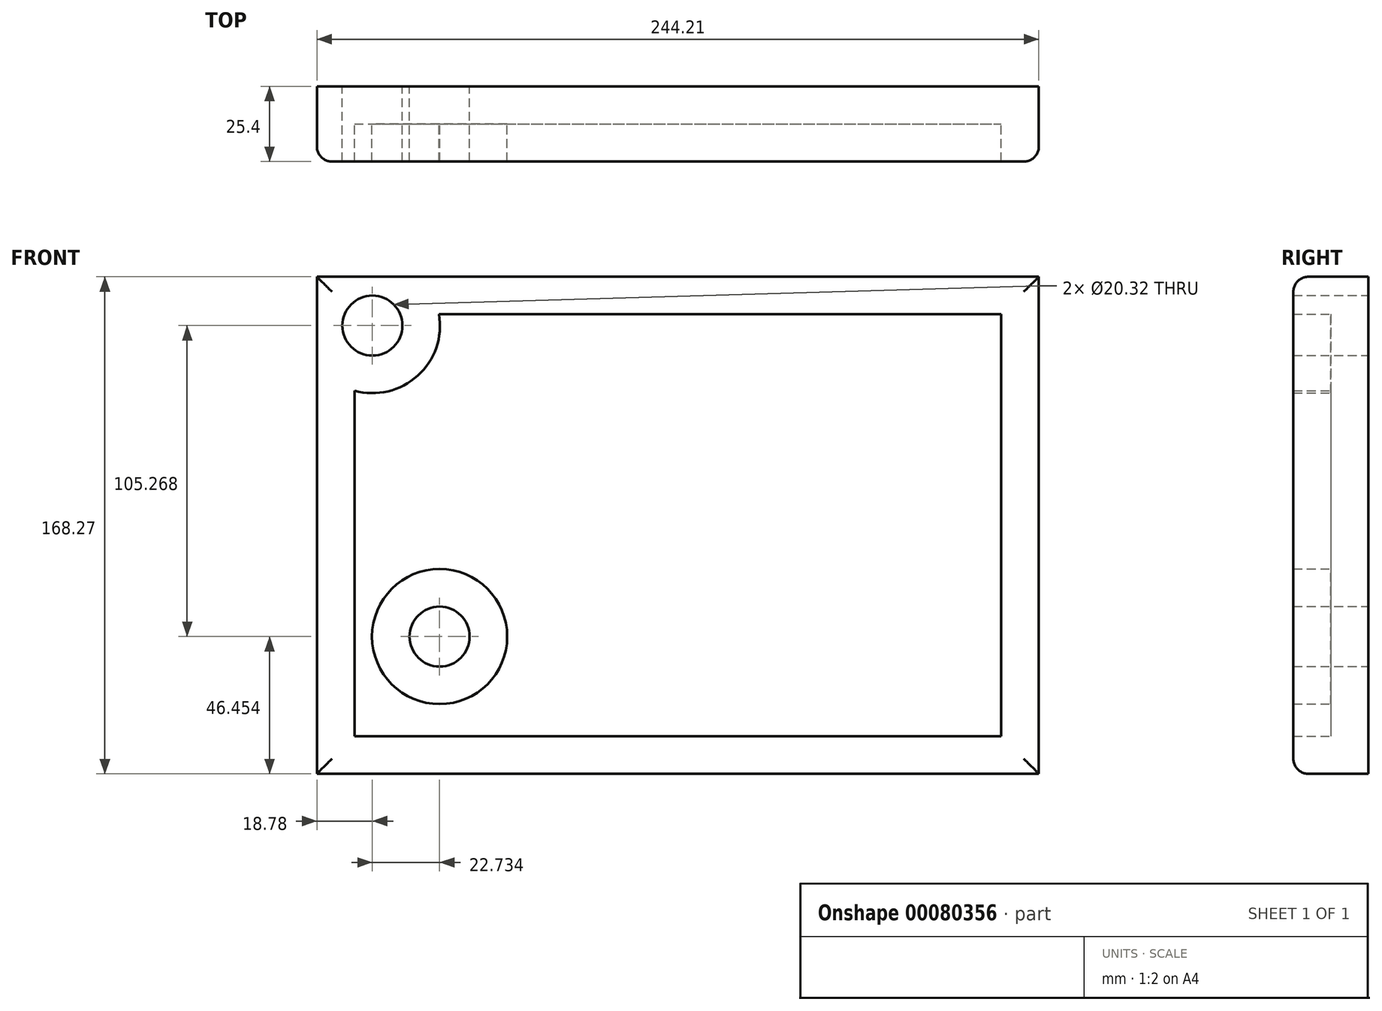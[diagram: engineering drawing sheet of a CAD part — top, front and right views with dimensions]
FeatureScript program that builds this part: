
annotation { "Feature Type Name" : "Feature", "Feature Type Description" : "" }
export const myFeature = defineFeature(function(context is Context, id is Id, definition is map)
    precondition{}
    {
        {
            var Q0;
            Q0=qCreatedBy(makeId("Front.planeOp"),FACE);
            var sketch = newSketch(context, id + "F0", { "sketchPlane" : qUnion([Q0])});
            skLineSegment(sketch, "E0.bottom", {"start": v(-105.93, 86.8) * mm, "end": v(138.28, 86.8) * mm});
            skLineSegment(sketch, "E0.top", {"start": v(-105.93, -81.47) * mm, "end": v(138.28, -81.47) * mm});
            skLineSegment(sketch, "E0.left", {"start": v(-105.93, 86.8) * mm, "end": v(-105.93, -81.47) * mm});
            skLineSegment(sketch, "E0.right", {"start": v(138.28, 86.8) * mm, "end": v(138.28, -81.47) * mm});
            skCircle(sketch, "E1", {"center": v(-87.15, 70.25) * mm, "radius": 10.16 * mm});
            skCircle(sketch, "E2", {"center": v(-64.42, -35.02) * mm, "radius": 10.16 * mm});
            skSolve(sketch);
        }
        {
            var Q0;
            Q0=makeQuery(id+"F0.imprint","IMPRINT",FACE,{"disambiguationData":[TD([[makeQuery(id+"F0.imprint","IMPRINT",EDGE,{"derivedFrom":sQuery(id+"F0.wireOp",EDGE,"E0.bottom")}),-1.0]])]});
            extrude(context, id + "F1", {"entities" : qUnion([Q0]), "depth" : 25.4 * mm});
        }
        {
            var Q0;
            Q0=makeQuery(id+"F1.opExtrude","CAP_EDGE",EDGE,{"disambiguationData":[OSD([sQuery(id+"F0.wireOp",EDGE,"E0.bottom")])],"isStart":false});
            var Q1;
            Q1=makeQuery(id+"F1.opExtrude","CAP_EDGE",EDGE,{"disambiguationData":[OSD([sQuery(id+"F0.wireOp",EDGE,"E0.left")])],"isStart":false});
            var Q2;
            Q2=makeQuery(id+"F1.opExtrude","CAP_EDGE",EDGE,{"disambiguationData":[OSD([sQuery(id+"F0.wireOp",EDGE,"E0.top")])],"isStart":false});
            var Q3;
            Q3=makeQuery(id+"F1.opExtrude","CAP_EDGE",EDGE,{"disambiguationData":[OSD([sQuery(id+"F0.wireOp",EDGE,"E0.right")])],"isStart":false});
            fillet(context, id + "F2", {"entities" : qUnion([Q0, Q1, Q2, Q3]), "radius" : 5.08 * mm, "tangentPropagation" : true, "allowEdgeOverflow" : false});
        }
        {
            var Q0;
            Q0=makeQuery(id+"F1.opExtrude","CAP_FACE",FACE,{"disambiguationData":[OSD([sQuery(id+"F0.wireOp",EDGE,"E0.bottom"),sQuery(id+"F0.wireOp",EDGE,"E0.top"),sQuery(id+"F0.wireOp",EDGE,"E0.left"),sQuery(id+"F0.wireOp",EDGE,"E0.right"),sQuery(id+"F0.wireOp",EDGE,"E1"),sQuery(id+"F0.wireOp",EDGE,"E2")])],"isStart":false});
            shell(context, id + "F3", {"entities" : qUnion([Q0]), "thickness" : 12.7 * mm});
        }
    });
